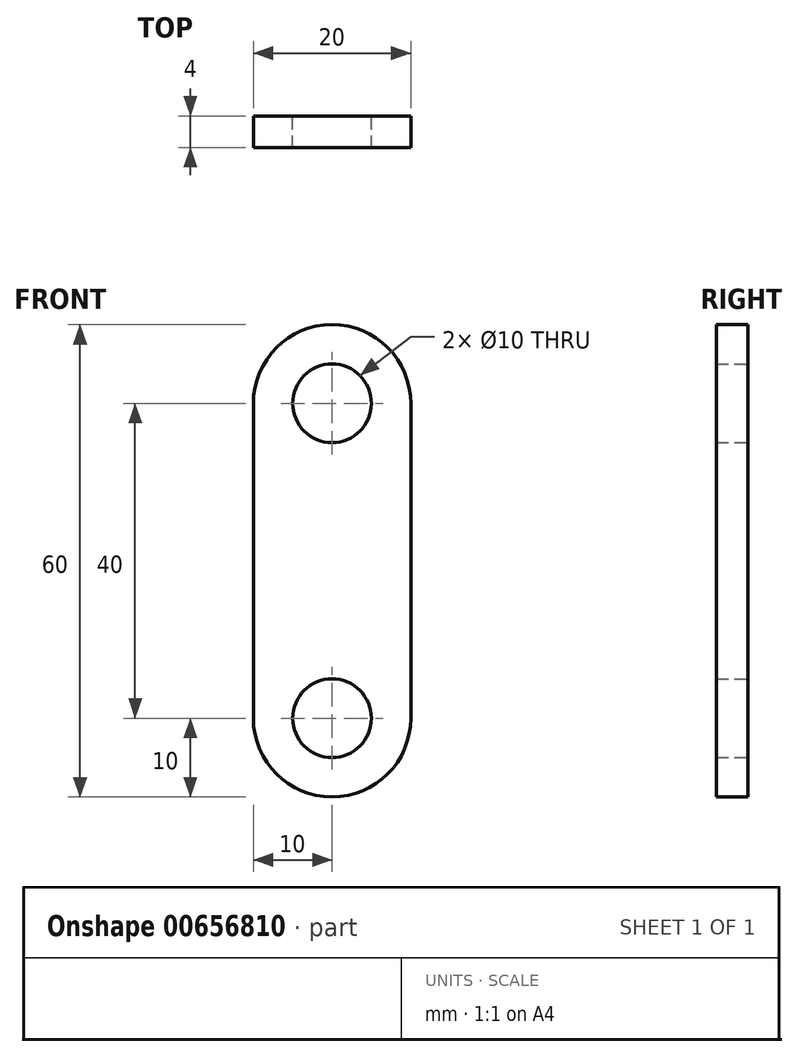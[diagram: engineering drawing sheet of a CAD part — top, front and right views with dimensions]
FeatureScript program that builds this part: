
annotation { "Feature Type Name" : "Feature", "Feature Type Description" : "" }
export const myFeature = defineFeature(function(context is Context, id is Id, definition is map)
    precondition{}
    {
        {
            var Q0;
            Q0=qCreatedBy(makeId("Front.planeOp"),FACE);
            var sketch = newSketch(context, id + "F0", { "sketchPlane" : qUnion([Q0])});
            skCircle(sketch, "E0", {"center": v(0, 0) * mm, "radius": 5 * mm});
            skLineSegment(sketch, "E1", {"start": v(0, 0) * mm, "end": v(0, -40) * mm, "construction": true});
            skCircle(sketch, "E2", {"center": v(0, -40) * mm, "radius": 5 * mm});
            skCircle(sketch, "E3", {"center": v(0, 0) * mm, "radius": 10 * mm});
            skCircle(sketch, "E4", {"center": v(0, -40) * mm, "radius": 10 * mm});
            skLineSegment(sketch, "E5", {"start": v(0, 0) * mm, "end": v(10, 0) * mm, "construction": true});
            skLineSegment(sketch, "E6", {"start": v(10, 0) * mm, "end": v(10, -40) * mm});
            skLineSegment(sketch, "E7.MirrorCS", {"start": v(-10, 0) * mm, "end": v(-10, -40) * mm});
            skSolve(sketch);
        }
        {
            var Q0;
            Q0=makeQuery(id+"F0.imprint","IMPRINT",FACE,{"disambiguationData":[TD([[makeQuery(id+"F0.imprint","IMPRINT",EDGE,{"derivedFrom":sQuery(id+"F0.wireOp",EDGE,"E0")}),-1.0]])]});
            var Q1;
            {var subQ0=sQuery(id+"F0.wireOp",EDGE,"E6");Q1=makeQuery(id+"F0.imprint","IMPRINT",FACE,{"disambiguationData":[TD([[makeQuery(id+"F0.imprint","IMPRINT",EDGE,{"derivedFrom":subQ0}),-1.0]])]});}
            var Q2;
            Q2=makeQuery(id+"F0.imprint","IMPRINT",FACE,{"disambiguationData":[TD([[makeQuery(id+"F0.imprint","IMPRINT",EDGE,{"derivedFrom":sQuery(id+"F0.wireOp",EDGE,"E2")}),-1.0]])]});
            extrude(context, id + "F1", {"entities" : qUnion([Q0, Q1, Q2]), "depth" : 4 * mm, "offsetDistance" : 25 * mm});
        }
    });
